# Revit family: FU_Modular_Sandler_Pau 1810PT
name_source: partatom
category: Furniture
units: mm (PartAtom-declared; Revit-internal decimal feet)

## family parameters
Always vertical = Yes
Cut with Voids When Loaded = No
OmniClass Number = 23.40.20.00
OmniClass Title = General Furniture and Specialties
Room Calculation Point = No
Shared = No
Work Plane-Based = No

## types (6) — shared parameters
Manufacturer = Sandler
Thickness = 50 mm  [stored 0.164042 ft]
URL = https://www.sandlerseating.com
zero-valued in all types: Default Elevation

## per-type parameters (varying)
| type | Description | Model | Overall Elevation | Panel Height | Width |
| PAU1810PT | Upholstered rear privacy screen for sofas and modules with backrest. | PAU1810PT | 1300 mm  [stored 4.26509 ft] | 1200 mm  [stored 3.93701 ft] | 600 mm  [stored 1.9685 ft] |
| ESC0824PT | Upholstered back side privacy panel. | Escalas 0824PT | 1200 mm  [stored 3.93701 ft] | 970 mm | 2400 mm |
| ESC0818PT | Upholstered back side privacy panel. | ESCALAS 0818PT | 1200 mm  [stored 3.93701 ft] | 970 mm | 1800 mm  [stored 5.90551 ft] |
| ESC0816PT | Upholstered back side privacy panel. | ESCALAS 0816PT | 1200 mm  [stored 3.93701 ft] | 970 mm | 1600 mm  [stored 5.24934 ft] |
| ESC0812PT | Upholstered back side privacy panel. | ESCALAS 0812PT | 1200 mm  [stored 3.93701 ft] | 970 mm | 1200 mm  [stored 3.93701 ft] |
| ESC0820PT | Upholstered back side privacy panel. | ESCALAS 0820PT | 1200 mm  [stored 3.93701 ft] | 970 mm | 2000 mm  [stored 6.56168 ft] |

note: [stored X ft] marks values corroborated as IEEE doubles in the binary element streams (Revit-internal decimal feet)

## geometry (parser evidence)
native form markers: Sweep x3
no freeform markers — native parametric forms only
